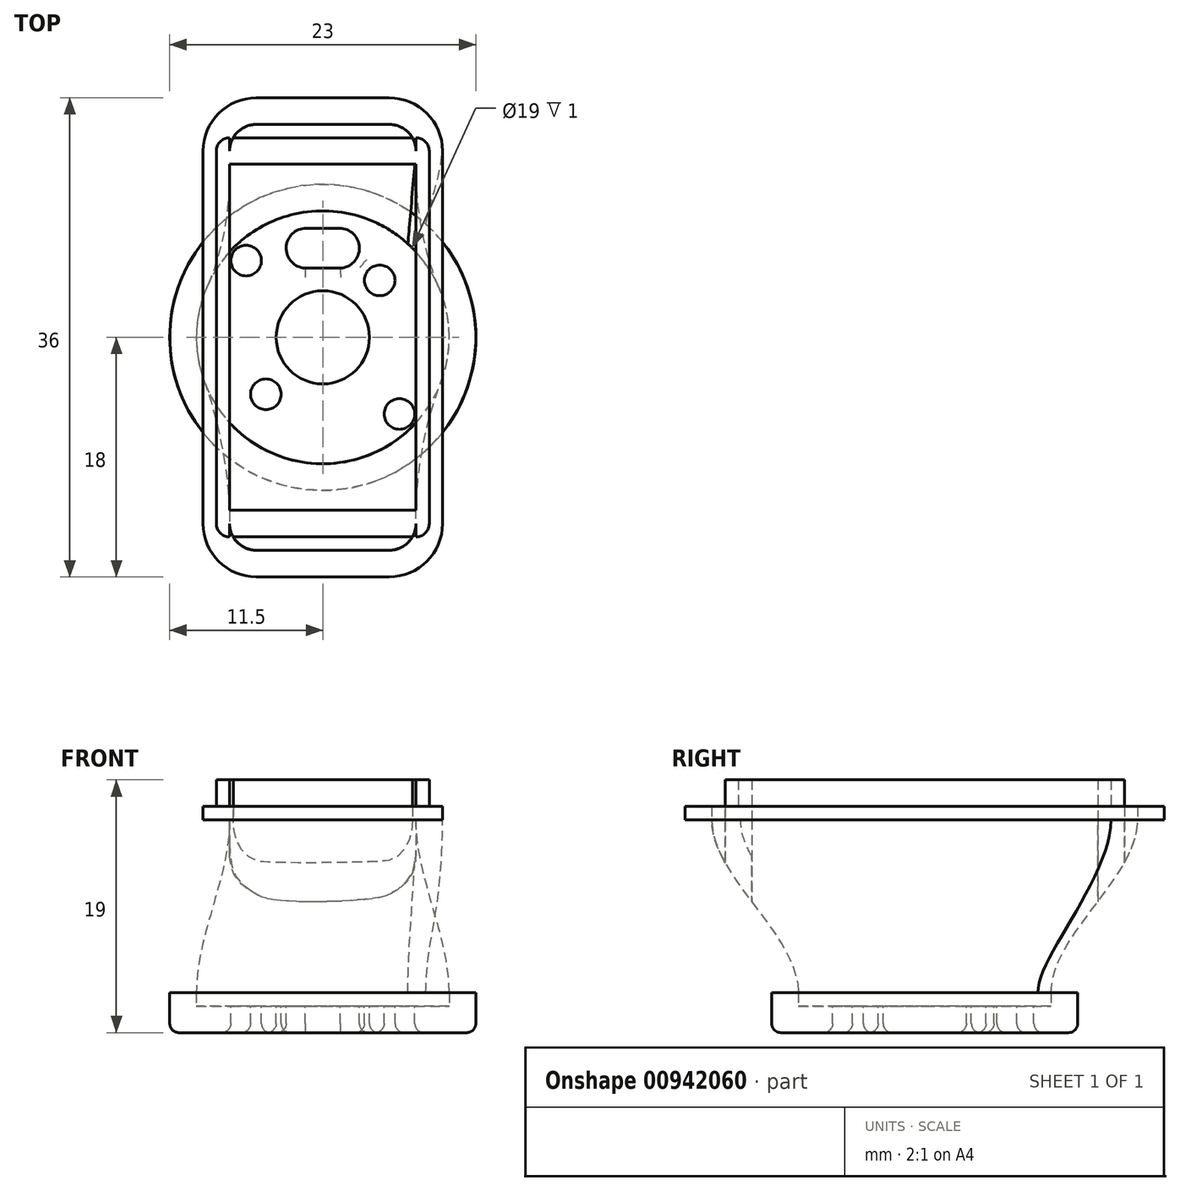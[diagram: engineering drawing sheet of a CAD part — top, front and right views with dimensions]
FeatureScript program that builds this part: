
annotation { "Feature Type Name" : "Feature", "Feature Type Description" : "" }
export const myFeature = defineFeature(function(context is Context, id is Id, definition is map)
    precondition{}
    {
        {
            var Q0;
            Q0=qCreatedBy(makeId("Top.planeOp"),FACE);
            var sketch = newSketch(context, id + "F0", { "sketchPlane" : qUnion([Q0])});
            skCircle(sketch, "E0", {"center": v(0, 0) * mm, "radius": 9.5 * mm});
            skSolve(sketch);
        }
        {
            var Q0;
            Q0=qCreatedBy(makeId("Top.planeOp"),FACE);
            var sketch = newSketch(context, id + "F1", { "sketchPlane" : qUnion([Q0])});
            skLineSegment(sketch, "E1.bottom", {"start": v(-5, 16) * mm, "end": v(5, 16) * mm});
            skLineSegment(sketch, "E1.top", {"start": v(-5, -16) * mm, "end": v(5, -16) * mm});
            skLineSegment(sketch, "E1.left", {"start": v(-7, 14) * mm, "end": v(-7, -14) * mm});
            skLineSegment(sketch, "E1.right", {"start": v(7, 14) * mm, "end": v(7, -14) * mm});
            skPoint(sketch, "E2.visualSharp", {"position": v(7, -16) * mm});
            skArc(sketch, "E2.filletArc", {"start": v(5, -16) * mm, "mid": v(6.41, -15.41) * mm, "end": v(7, -14) * mm});
            skPoint(sketch, "E3.visualSharp", {"position": v(-7, -16) * mm});
            skArc(sketch, "E3.filletArc", {"start": v(-7, -14) * mm, "mid": v(-6.41, -15.41) * mm, "end": v(-5, -16) * mm});
            skPoint(sketch, "E4.visualSharp", {"position": v(-7, 16) * mm});
            skArc(sketch, "E4.filletArc", {"start": v(-5, 16) * mm, "mid": v(-6.41, 15.41) * mm, "end": v(-7, 14) * mm});
            skPoint(sketch, "E5.visualSharp", {"position": v(7, 16) * mm});
            skArc(sketch, "E5.filletArc", {"start": v(7, 14) * mm, "mid": v(6.41, 15.41) * mm, "end": v(5, 16) * mm});
            skSolve(sketch);
        }
        {
            var Q0;
            Q0=makeQuery(id+"F1.imprint","IMPRINT",FACE,{"disambiguationData":[TD([[makeQuery(id+"F1.imprint","IMPRINT",EDGE,{"derivedFrom":sQuery(id+"F1.wireOp",EDGE,"E1.bottom")}),-1.0]])]});
            extrude(context, id + "F2", {"entities" : qUnion([Q0]), "depth" : 15 * mm, "offsetDistance" : 25 * mm, "hasSecondDirection" : true, "secondDirectionOppositeDirection" : false, "secondDirectionDepth" : 14 * mm});
        }
        {
            var Q0;
            Q0 = qSketchRegion(id + "F0", true);
            extrude(context, id + "F3", {"entities" : qUnion([Q0]), "depth" : 1 * mm, "offsetDistance" : 25 * mm});
        }
        {
            var Q0;
            Q0=makeQuery(id+"F3.opExtrude","CAP_FACE",FACE,{"disambiguationData":[OSD([sQuery(id+"F0.wireOp",EDGE,"E0")])],"isStart":false});
            var sketch = newSketch(context, id + "F4", { "sketchPlane" : qUnion([Q0])});
            skArc(sketch, "E6", {"start": v(6.4, 7.03) * mm, "mid": v(4.8, 8.2) * mm, "end": v(3, 9.01) * mm});
            skArc(sketch, "E7", {"start": v(-6.13, 7.25) * mm, "mid": v(-9.49, 0.52) * mm, "end": v(-6.89, -6.54) * mm});
            skArc(sketch, "E8", {"start": v(-6.89, -6.54) * mm, "mid": v(-4.77, -8.22) * mm, "end": v(-2.26, -9.23) * mm});
            skArc(sketch, "E9", {"start": v(6.8, -6.64) * mm, "mid": v(9.5, 0.28) * mm, "end": v(6.4, 7.03) * mm});
            skLineSegment(sketch, "E10", {"start": v(0, 0) * mm, "end": v(22.9, 0) * mm, "construction": true});
            skArc(sketch, "E11", {"start": v(3.37, -8.88) * mm, "mid": v(5.2, -7.95) * mm, "end": v(6.8, -6.64) * mm});
            skArc(sketch, "E12", {"start": v(3, 9.01) * mm, "mid": v(0.46, 9.49) * mm, "end": v(-2.12, 9.26) * mm});
            skArc(sketch, "E13", {"start": v(-2.12, 9.26) * mm, "mid": v(-4.25, 8.5) * mm, "end": v(-6.13, 7.25) * mm});
            skArc(sketch, "E14", {"start": v(-2.26, -9.23) * mm, "mid": v(0.58, -9.48) * mm, "end": v(3.37, -8.88) * mm});
            skSolve(sketch);
        }
        {
            var Q1;
            Q1=makeQuery(id+"F4.imprint","IMPRINT",FACE,{"disambiguationData":[TD([[makeQuery(id+"F4.imprint","IMPRINT",EDGE,{"derivedFrom":sQuery(id+"F4.wireOp",EDGE,"E6")}),1.0]])]});
            var Q2;
            Q2=makeQuery(id+"F2.opExtrude","CAP_FACE",FACE,{"disambiguationData":[OSD([sQuery(id+"F1.wireOp",EDGE,"E1.bottom"),sQuery(id+"F1.wireOp",EDGE,"E1.top"),sQuery(id+"F1.wireOp",EDGE,"E1.left"),sQuery(id+"F1.wireOp",EDGE,"E1.right")])],"isStart":true});
            loft(context, id + "F5", {"operationType" : NewBodyOperationType.ADD, "startCondition" : LoftEndDerivativeType.NORMAL_TO_PROFILE, "startMagnitude" : 1, "endCondition" : LoftEndDerivativeType.NORMAL_TO_PROFILE, "endMagnitude" : 1, "sheetProfilesArray" : [{ "sheetProfileEntities" : qUnion([Q1]) }, { "sheetProfileEntities" : qUnion([Q2]) }]});
        }
        {
            var Q0;
            Q0=makeQuery(id+"F2.opExtrude","CAP_FACE",FACE,{"disambiguationData":[OSD([sQuery(id+"F1.wireOp",EDGE,"E1.bottom"),sQuery(id+"F1.wireOp",EDGE,"E1.top"),sQuery(id+"F1.wireOp",EDGE,"E1.left"),sQuery(id+"F1.wireOp",EDGE,"E1.right"),sQuery(id+"F1.wireOp",EDGE,"E2.filletArc"),sQuery(id+"F1.wireOp",EDGE,"E3.filletArc"),sQuery(id+"F1.wireOp",EDGE,"E4.filletArc"),sQuery(id+"F1.wireOp",EDGE,"E5.filletArc")])],"isStart":false});
            shell(context, id + "F6", {"entities" : qUnion([Q0]), "thickness" : 2 * mm, "oppositeDirection" : true});
        }
        {
            var Q0;
            Q0=makeQuery(id+"F2.opExtrude","CAP_FACE",FACE,{"disambiguationData":[OSD([sQuery(id+"F1.wireOp",EDGE,"E1.bottom"),sQuery(id+"F1.wireOp",EDGE,"E1.top"),sQuery(id+"F1.wireOp",EDGE,"E1.left"),sQuery(id+"F1.wireOp",EDGE,"E1.right"),sQuery(id+"F1.wireOp",EDGE,"E2.filletArc"),sQuery(id+"F1.wireOp",EDGE,"E3.filletArc"),sQuery(id+"F1.wireOp",EDGE,"E4.filletArc"),sQuery(id+"F1.wireOp",EDGE,"E5.filletArc")])],"isStart":false});
            var sketch = newSketch(context, id + "F7", { "sketchPlane" : qUnion([Q0])});
            skLineSegment(sketch, "E15.0", {"start": v(9, 14) * mm, "end": v(9, -14) * mm});
            skLineSegment(sketch, "E16.0", {"start": v(-5, -18) * mm, "end": v(5, -18) * mm});
            skFitSpline(sketch, "E17.0", {"points": [v(-9, 14) * mm, v(-9, 4.67) * mm, v(-9, -4.67) * mm, v(-9, -14) * mm]});
            skLineSegment(sketch, "E18.0", {"start": v(-5, 18) * mm, "end": v(5, 18) * mm});
            skLineSegment(sketch, "E19.0", {"start": v(8, 15) * mm, "end": v(8, -15) * mm});
            skLineSegment(sketch, "E20.0", {"start": v(-8, -15) * mm, "end": v(8, -15) * mm});
            skLineSegment(sketch, "E21.0", {"start": v(-8, 15) * mm, "end": v(8, 15) * mm});
            skFitSpline(sketch, "E22.0", {"points": [v(-8, 13) * mm, v(-8, 4.33) * mm, v(-8, -4.33) * mm, v(-8, -13) * mm]});
            skLineSegment(sketch, "E23", {"start": v(-8, -13) * mm, "end": v(-8, -15) * mm});
            skLineSegment(sketch, "E24", {"start": v(-8, 13) * mm, "end": v(-8, 15) * mm});
            skFitSpline(sketch, "E25.0", {"points": [v(-9, 14) * mm, v(-9, 4.67) * mm, v(-9, -4.67) * mm, v(-9, -14) * mm]});
            skLineSegment(sketch, "E26.0", {"start": v(7, 15) * mm, "end": v(7, -15) * mm});
            skFitSpline(sketch, "E27.0", {"points": [v(-7, 14) * mm, v(-7, 4.67) * mm, v(-7, -4.67) * mm, v(-7, -14) * mm]});
            skLineSegment(sketch, "E28", {"start": v(-7, 13) * mm, "end": v(-7, 15) * mm});
            skLineSegment(sketch, "E29", {"start": v(-7, -13) * mm, "end": v(-7, -15) * mm});
            skLineSegment(sketch, "E30", {"start": v(-7, -13) * mm, "end": v(7, -13) * mm});
            skLineSegment(sketch, "E31", {"start": v(-7, 13) * mm, "end": v(7, 13) * mm});
            skSolve(sketch);
        }
        {
            var Q0;
            Q0=makeQuery(id+"F7.imprint","IMPRINT",FACE,{"disambiguationData":[TD([[makeQuery(id+"F7.imprint","IMPRINT",EDGE,{"derivedFrom":sQuery(id+"F7.wireOp",EDGE,"E22.0")}),1.0]])]});
            var Q1;
            {var subQ0=makeQuery(id+"F6.opShell","OFFSET_EDGE",EDGE,{"disambiguationData":[OSD([sQuery(id+"F1.wireOp",EDGE,"E1.left")])]});Q1=makeQuery(id+"F7.imprint","IMPRINT",FACE,{"disambiguationData":[TD([[makeQuery(id+"F7.imprint","IMPRINT",EDGE,{"derivedFrom":subQ0}),1.0]])]});}
            var Q2;
            {var subQ2=sQuery(id+"F7.wireOp",EDGE,"E19.0");Q2=makeQuery(id+"F7.imprint","IMPRINT",FACE,{"disambiguationData":[TD([[makeQuery(id+"F7.imprint","IMPRINT",EDGE,{"derivedFrom":subQ2}),-1.0]])]});}
            extrude(context, id + "F8", {"entities" : qUnion([Q0, Q1, Q2]), "operationType" : NewBodyOperationType.ADD, "depth" : 2 * mm, "offsetDistance" : 25 * mm});
        }
        {
            var Q0;
            Q0=makeQuery(id+"F7.imprint","IMPRINT",FACE,{"disambiguationData":[TD([[makeQuery(id+"F7.imprint","IMPRINT",EDGE,{"derivedFrom":sQuery(id+"F7.wireOp",EDGE,"E22.0")}),1.0]])]});
            var Q1;
            {var subQ4=sQuery(id+"F7.wireOp",EDGE,"E19.0");Q1=makeQuery(id+"F7.imprint","IMPRINT",FACE,{"disambiguationData":[TD([[makeQuery(id+"F7.imprint","IMPRINT",EDGE,{"derivedFrom":subQ4}),-1.0]])]});}
            extrude(context, id + "F9", {"entities" : qUnion([Q0, Q1]), "operationType" : NewBodyOperationType.ADD, "depth" : 2 * mm, "offsetDistance" : 25 * mm});
        }
        {
            var Q0;
            {var subQ0=sQuery(id+"F7.wireOp",EDGE,"E30");Q0=makeQuery(id+"F7.imprint","IMPRINT",FACE,{"disambiguationData":[TD([[makeQuery(id+"F7.imprint","IMPRINT",EDGE,{"derivedFrom":subQ0}),-1.0]])]});}
            var Q1;
            {var subQ0=sQuery(id+"F7.wireOp",EDGE,"E31");Q1=makeQuery(id+"F7.imprint","IMPRINT",FACE,{"disambiguationData":[TD([[makeQuery(id+"F7.imprint","IMPRINT",EDGE,{"derivedFrom":subQ0}),1.0]])]});}
            extrude(context, id + "F10", {"entities" : qUnion([Q0, Q1]), "operationType" : NewBodyOperationType.ADD, "depth" : 2 * mm, "offsetDistance" : 25 * mm, "hasSecondDirection" : true, "secondDirectionBound" : SecondDirectionBoundingType.UP_TO_NEXT, "secondDirectionOppositeDirection" : true, "secondDirectionDepth" : 25 * mm});
        }
        {
            var Q0;
            Q0=makeQuery(id+"F8.opExtrude","SWEPT_EDGE",EDGE,{"disambiguationData":[OSD([sQuery(id+"F7.wireOp",EDGE,"E19.0"),sQuery(id+"F7.wireOp",EDGE,"E20.0")])]});
            var Q1;
            Q1=makeQuery(id+"F8.opExtrude","SWEPT_EDGE",EDGE,{"disambiguationData":[OSD([sQuery(id+"F7.wireOp",EDGE,"E20.0"),sQuery(id+"F7.wireOp",EDGE,"E23")])]});
            var Q2;
            Q2=makeQuery(id+"F8.opExtrude","SWEPT_EDGE",EDGE,{"disambiguationData":[OSD([sQuery(id+"F7.wireOp",EDGE,"E19.0"),sQuery(id+"F7.wireOp",EDGE,"E21.0")])]});
            var Q3;
            Q3=makeQuery(id+"F8.opExtrude","SWEPT_EDGE",EDGE,{"disambiguationData":[OSD([sQuery(id+"F7.wireOp",EDGE,"E21.0"),sQuery(id+"F7.wireOp",EDGE,"E24")])]});
            fillet(context, id + "F11", {"entities" : qUnion([Q0, Q1, Q2, Q3]), "radius" : 1 * mm, "tangentPropagation" : true, "allowEdgeOverflow" : false});
        }
        {
            var Q0;
            {var subQ0=sQuery(id+"F0.wireOp",EDGE,"E0");Q0=makeQuery(id+"F6.opShell","OFFSET_FACE",FACE,{"disambiguationData":[OSD([subQ0]),TDD([makeQuery(id+"F3.opExtrude","CAP_FACE",FACE,{"disambiguationData":[OSD([subQ0])],"isStart":true})])]});}
            var sketch = newSketch(context, id + "F12", { "sketchPlane" : qUnion([Q0])});
            skPoint(sketch, "E32.0", {"position": v(0, 0) * mm});
            skCircle(sketch, "E33", {"center": v(0, 0) * mm, "radius": 3.5 * mm});
            skCircle(sketch, "E34", {"center": v(0, 0) * mm, "radius": 6.05 * mm, "construction": true});
            skCircle(sketch, "E35", {"center": v(0, 0) * mm, "radius": 8.15 * mm, "construction": true});
            skLineSegment(sketch, "E36", {"start": v(0, 0) * mm, "end": v(6.04, 6.04) * mm, "construction": true});
            skLineSegment(sketch, "E37", {"start": v(0, 0) * mm, "end": v(-6.07, 6.07) * mm, "construction": true});
            skCircle(sketch, "E38", {"center": v(4.28, 4.28) * mm, "radius": 1.15 * mm});
            skCircle(sketch, "E39", {"center": v(-5.76, 5.76) * mm, "radius": 1.15 * mm});
            skArc(sketch, "E40", {"start": v(1.32, 5.2) * mm, "mid": v(2.75, 6.73) * mm, "end": v(1.25, 8.2) * mm});
            skArc(sketch, "E41.MirrorC", {"start": v(-1.32, 5.2) * mm, "mid": v(-2.75, 6.74) * mm, "end": v(-1.24, 8.2) * mm});
            skLineSegment(sketch, "E42", {"start": v(-1.26, 8.2) * mm, "end": v(1.25, 8.2) * mm});
            skPoint(sketch, "E43.orphan", {"position": v(0, 5) * mm});
            skLineSegment(sketch, "E44", {"start": v(-1.32, 5.2) * mm, "end": v(1.32, 5.2) * mm});
            skCircle(sketch, "E45.1.0", {"center": v(-4.28, -4.28) * mm, "radius": 1.15 * mm});
            skCircle(sketch, "E45.1.1", {"center": v(5.76, -5.76) * mm, "radius": 1.15 * mm});
            skSolve(sketch);
        }
        {
            var Q0;
            {var subQ1=sQuery(id+"F12.wireOp",EDGE,"E40");Q0=makeQuery(id+"F12.imprint","IMPRINT",FACE,{"disambiguationData":[TD([[makeQuery(id+"F12.imprint","IMPRINT",EDGE,{"derivedFrom":subQ1}),1.0]])]});}
            var Q1;
            Q1=makeQuery(id+"F12.imprint","IMPRINT",FACE,{"disambiguationData":[TD([[makeQuery(id+"F12.imprint","IMPRINT",EDGE,{"derivedFrom":sQuery(id+"F12.wireOp",EDGE,"E39")}),1.0]])]});
            var Q2;
            Q2=makeQuery(id+"F12.imprint","IMPRINT",FACE,{"disambiguationData":[TD([[makeQuery(id+"F12.imprint","IMPRINT",EDGE,{"derivedFrom":sQuery(id+"F12.wireOp",EDGE,"E45.1.0")}),1.0]])]});
            var Q3;
            Q3=makeQuery(id+"F12.imprint","IMPRINT",FACE,{"disambiguationData":[TD([[makeQuery(id+"F12.imprint","IMPRINT",EDGE,{"derivedFrom":sQuery(id+"F12.wireOp",EDGE,"E45.1.1")}),1.0]])]});
            var Q4;
            Q4=makeQuery(id+"F12.imprint","IMPRINT",FACE,{"disambiguationData":[TD([[makeQuery(id+"F12.imprint","IMPRINT",EDGE,{"derivedFrom":sQuery(id+"F12.wireOp",EDGE,"E38")}),1.0]])]});
            var Q5;
            Q5=makeQuery(id+"F12.imprint","IMPRINT",FACE,{"disambiguationData":[TD([[makeQuery(id+"F12.imprint","IMPRINT",EDGE,{"derivedFrom":sQuery(id+"F12.wireOp",EDGE,"E33")}),1.0]])]});
            extrude(context, id + "F13", {"entities" : qUnion([Q0, Q1, Q2, Q3, Q4, Q5]), "operationType" : NewBodyOperationType.REMOVE, "oppositeDirection" : true, "depth" : 3 * mm, "offsetDistance" : 25 * mm});
        }
        {
            var Q0;
            Q0=makeQuery(id+"F3.opExtrude","CAP_FACE",FACE,{"disambiguationData":[OSD([sQuery(id+"F0.wireOp",EDGE,"E0")])],"isStart":true});
            var Q1;
            Q1=makeQuery(id+"F13.boolean.opBoolean","COPY",EDGE,{"derivedFrom":makeQuery(id+"F13.opExtrude","CAP_EDGE",EDGE,{"disambiguationData":[OSD([sQuery(id+"F12.wireOp",EDGE,"E44")])],"isStart":true})});
            var Q2;
            Q2=makeQuery(id+"F13.boolean.opBoolean","COPY",EDGE,{"derivedFrom":makeQuery(id+"F13.opExtrude","CAP_EDGE",EDGE,{"disambiguationData":[OSD([sQuery(id+"F12.wireOp",EDGE,"E42")])],"isStart":true})});
            fillet(context, id + "F14", {"entities" : qUnion([Q0, Q1, Q2]), "radius" : 0.7 * mm, "tangentPropagation" : true, "allowEdgeOverflow" : false});
        }
    });
